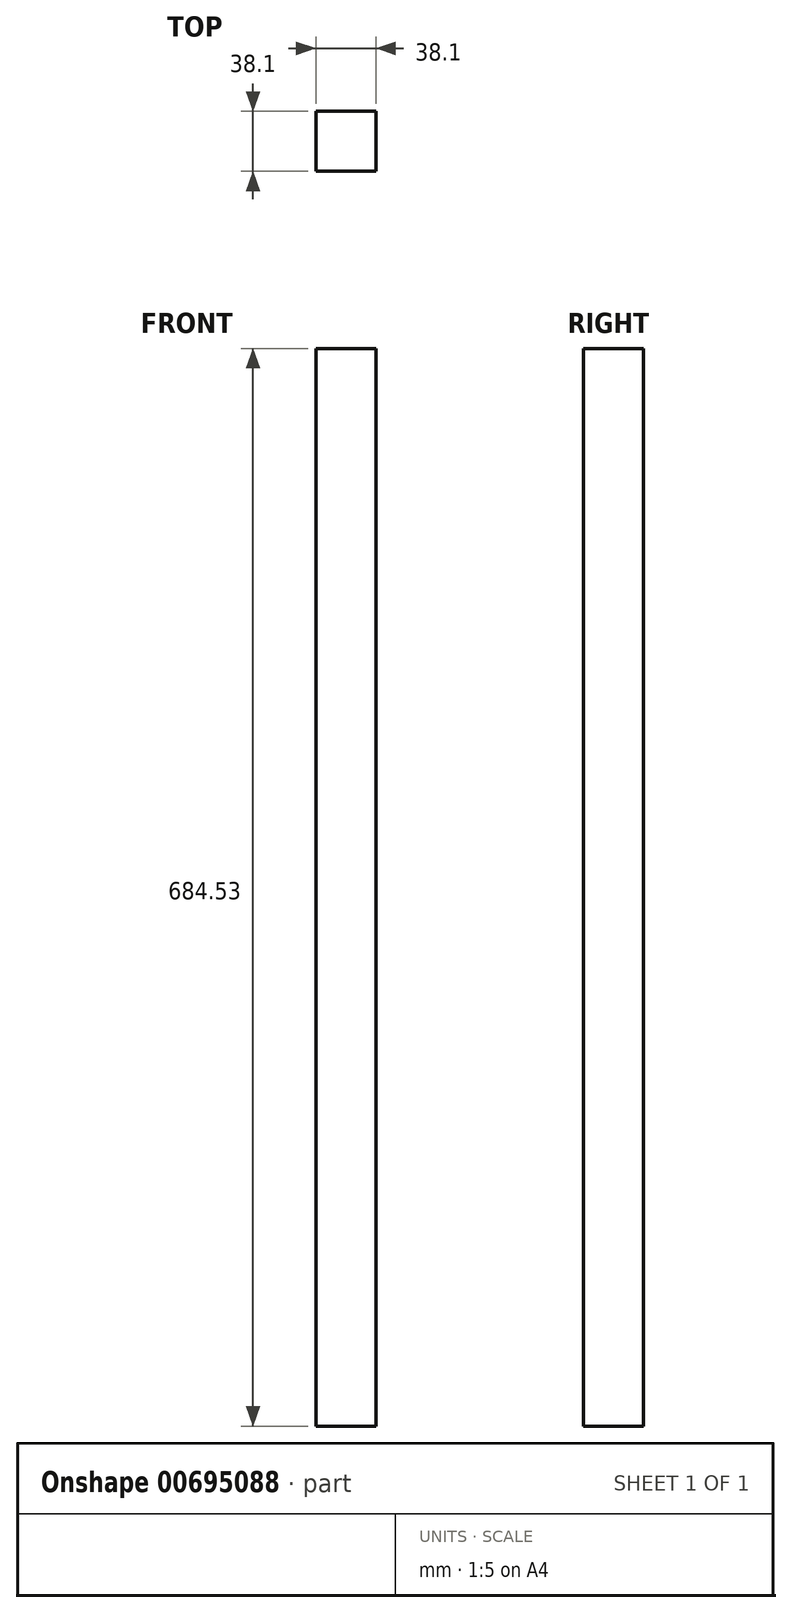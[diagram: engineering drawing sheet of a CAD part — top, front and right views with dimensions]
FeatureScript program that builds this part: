
annotation { "Feature Type Name" : "Feature", "Feature Type Description" : "" }
export const myFeature = defineFeature(function(context is Context, id is Id, definition is map)
    precondition{}
    {
        {
            var Q0;
            Q0=qCreatedBy(makeId("Top.planeOp"),FACE);
            var sketch = newSketch(context, id + "F0", { "sketchPlane" : qUnion([Q0])});
            skLineSegment(sketch, "E0.bottom", {"start": v(0, 0) * mm, "end": v(38.1, 0) * mm});
            skLineSegment(sketch, "E0.top", {"start": v(0, 38.1) * mm, "end": v(38.1, 38.1) * mm});
            skLineSegment(sketch, "E0.left", {"start": v(0, 0) * mm, "end": v(0, 38.1) * mm});
            skLineSegment(sketch, "E0.right", {"start": v(38.1, 0) * mm, "end": v(38.1, 38.1) * mm});
            skSolve(sketch);
        }
        {
            var Q0;
            Q0=makeQuery(id+"F0.imprint","IMPRINT",FACE,{"disambiguationData":[TD([[makeQuery(id+"F0.imprint","IMPRINT",EDGE,{"derivedFrom":sQuery(id+"F0.wireOp",EDGE,"E0.bottom")}),1.0]])]});
            extrude(context, id + "F1", {"entities" : qUnion([Q0]), "depth" : 684.53 * mm, "offsetDistance" : 25.4 * mm});
        }
    });
